# Revit family: Joist_NewMillennium_DLH-Series_SglPitch
name_source: partatom
category: Structural Framing
units: mm (PartAtom-declared; Revit-internal decimal feet)

## family parameters
Always export as geometry = No
Always vertical = Yes
Classification Number = 23.25.30.21.14.11
Cut with Voids When Loaded = No
Material for Model Behavior = Steel
Section Shape = Not Defined
Shared = No
Show family pre-cut in plan views = Yes

## types (12) — shared parameters
Assembly Code = B1010350
Bearing Seat = Yes
Bottom Chord Offset from End = 2' - 9 1/2"
Building Codes = https://www.newmill.com
Channel Width = 0' - 1 1/8"
Construction Details = https://www.newmill.com
Description = New Millennium Building Systems DLH Series - Single Pitch
Green Building-LEED = http://www.arcat.com
Installation-Fabrication = https://www.newmill.com
Keynote = 05 21 00
Lower Chord Representation = Metal - Steel
Manufacturer = New Millennium Building Systems
Manufacturer Fax = 260-868-6002
Manufacturer Website = https://www.newmill.com
Model = DLH Series - Single Pitch
Product Data = http://www.arcat.com
Revision = R0_10-2017
Roundover = 0' - 0 1/4"
Sales Information = https://www.newmill.com
Seat Length = 1' - 0"
SeatWdth = 0' - 2 1/8"
Specification = http://www.arcat.com
TXTLocation = 0' - 4"
Test Data = https://www.newmill.com
Thickness = 0' - 0 1/2"
Thickness_Channel = 0' - 0 3/16"
Type Comments = Contact New Millennium for Structural Web Design
URL = https://www.newmill.com
Upper Chord Representation = Metal - Steel
Web Infill = Metal - Steel

## per-type parameters (varying)
| type | Angle Size_Lower | Angle Size_Upper | Beam Depth | Max Length | SeatHalf |
| 52 in Depth / 104 Ft Max Length | 0' - 3 1/2" | 0' - 3 1/2" | 4' - 4" | 104' - 0" | 0' - 4 1/16" |
| 56 in Depth / 112 Ft Max Length | 0' - 3 1/2" | 0' - 3 1/2" | 4' - 8" | 112' - 0" | 0' - 4 1/16" |
| 60 in Depth / 120 Ft Max Length | 0' - 4" | 0' - 4" | 5' - 0" | 120' - 0" | 0' - 4 9/16" |
| 64 in Depth / 128 Ft Max Length | 0' - 6" | 0' - 6" | 5' - 4" | 128' - 0" | 0' - 6 9/16" |
| 68 in Depth / 136 Ft Max Length | 0' - 6" | 0' - 6" | 5' - 8" | 136' - 0" | 0' - 6 9/16" |
| 72 in Depth / 144 Ft Max Length | 0' - 6" | 0' - 6" | 6' - 0" | 144' - 0" | 0' - 6 9/16" |
| 80 in Depth / 160 Ft Max Length | 0' - 6" | 0' - 6" | 6' - 8" | 160' - 0" | 0' - 6 9/16" |
| 88 in Depth / 176 Ft Max Length | 0' - 6" | 0' - 6" | 7' - 4" | 176' - 0" | 0' - 6 9/16" |
| 96 in Depth / 192 Ft Max Length | 0' - 6" | 0' - 6" | 8' - 0" | 192' - 0" | 0' - 6 9/16" |
| 104 in Depth / 208 Ft Max Length | 0' - 6" | 0' - 6" | 8' - 8" | 208' - 0" | 0' - 6 9/16" |
| 112 in Depth / 224 Ft Max Length | 0' - 6" | 0' - 6" | 9' - 4" | 224' - 0" | 0' - 6 9/16" |
| 120 in Depth / 240 Ft Max Length | 0' - 6" | 0' - 6" | 10' - 0" | 240' - 0" | 0' - 6 9/16" |

## geometry (parser evidence)
native form markers: Sweep x4
no freeform markers — native parametric forms only
